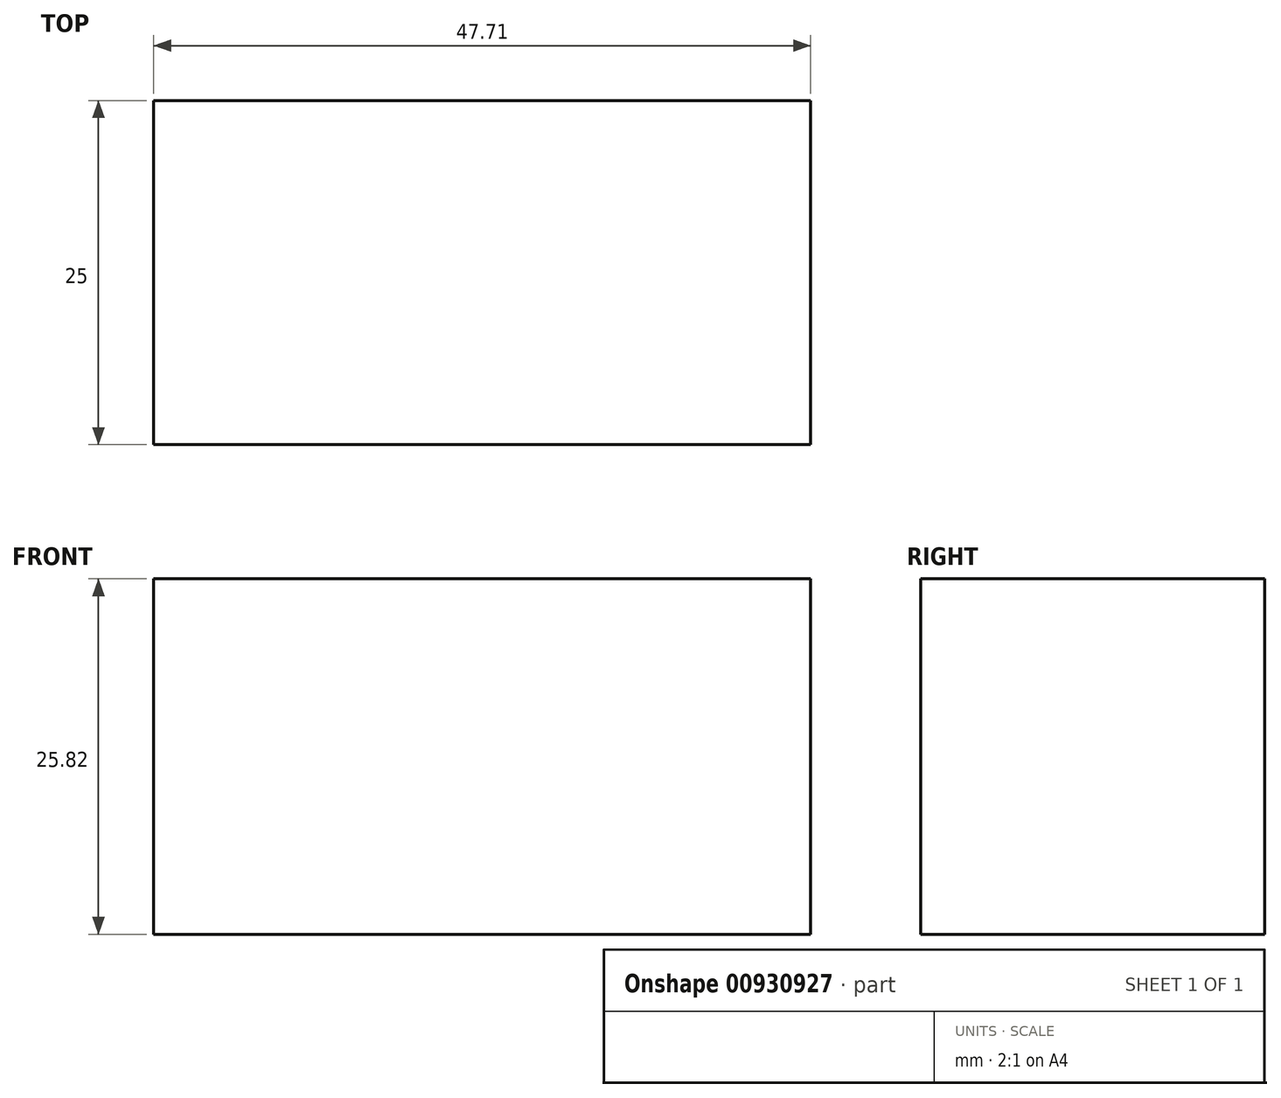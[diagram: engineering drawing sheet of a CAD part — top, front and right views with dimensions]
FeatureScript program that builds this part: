
annotation { "Feature Type Name" : "Feature", "Feature Type Description" : "" }
export const myFeature = defineFeature(function(context is Context, id is Id, definition is map)
    precondition{}
    {
        {
            var Q0;
            Q0=qCreatedBy(makeId("Front.planeOp"),FACE);
            cPlane(context, id + "F0", {"entities" : qUnion([Q0]), "cplaneType" : CPlaneType.OFFSET, "offset" : 90.1 * mm, "width" : 150 * mm, "height" : 150 * mm});
        }
        {
            var Q0;
            Q0=qCreatedBy(makeId("Front.planeOp"),FACE);
            var sketch = newSketch(context, id + "F1", { "sketchPlane" : qUnion([Q0])});
            skLineSegment(sketch, "E0.bottom", {"start": v(-117.98, 48.22) * mm, "end": v(-70.27, 48.22) * mm});
            skLineSegment(sketch, "E0.top", {"start": v(-117.98, 22.4) * mm, "end": v(-70.27, 22.4) * mm});
            skLineSegment(sketch, "E0.left", {"start": v(-117.98, 48.22) * mm, "end": v(-117.98, 22.4) * mm});
            skLineSegment(sketch, "E0.right", {"start": v(-70.27, 48.22) * mm, "end": v(-70.27, 22.4) * mm});
            skSolve(sketch);
        }
        {
            var Q0;
            Q0 = qSketchRegion(id + "F1", true);
            extrude(context, id + "F2", {"entities" : qUnion([Q0]), "depth" : 25 * mm, "offsetDistance" : 25 * mm});
        }
    });
